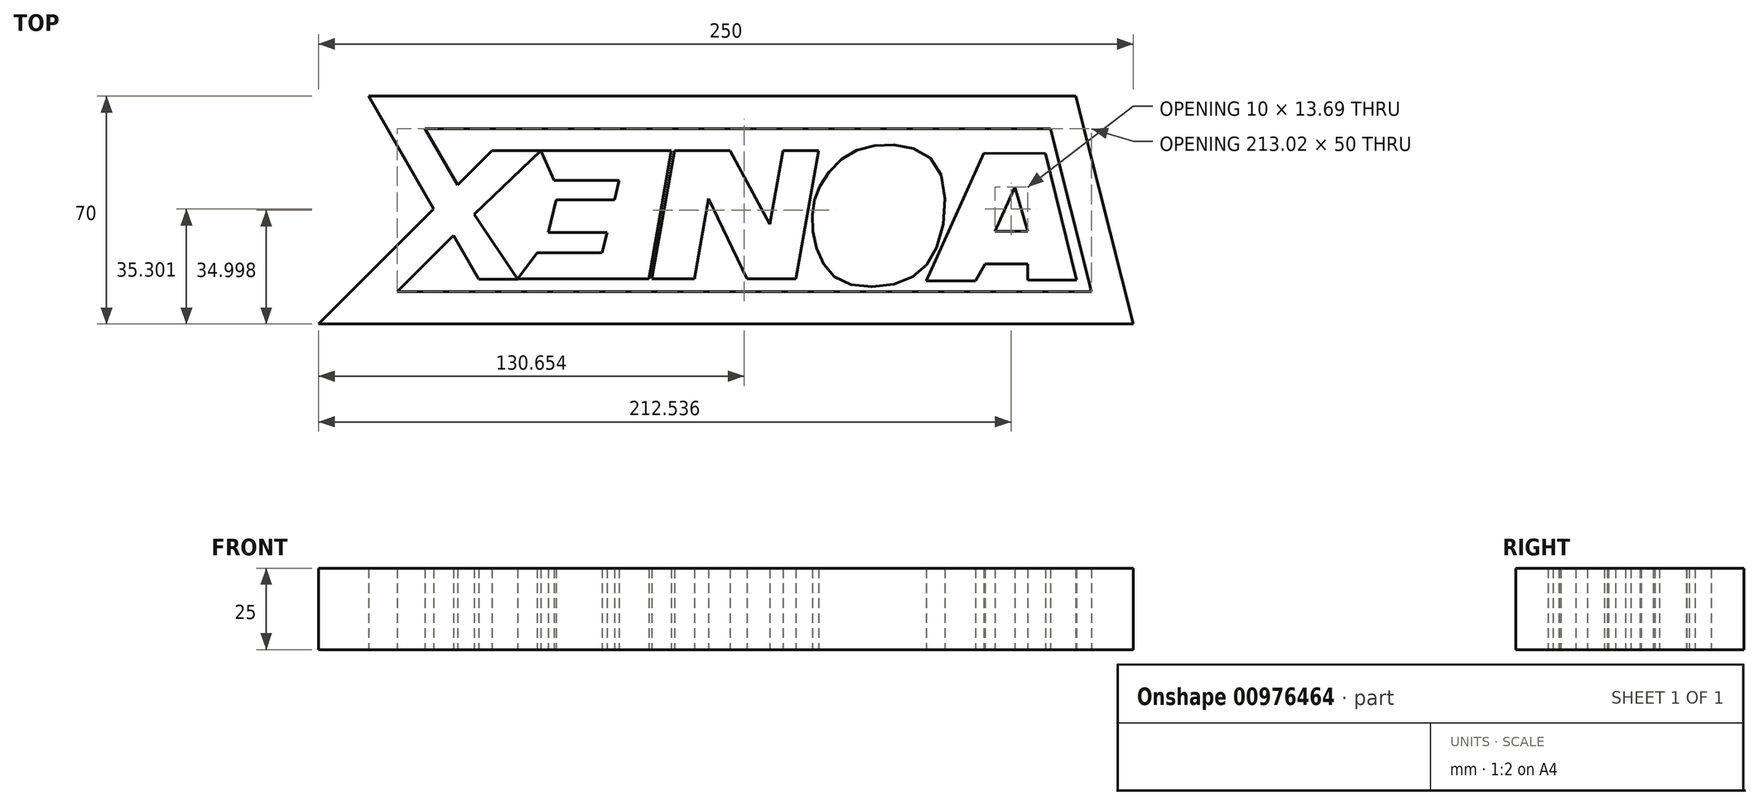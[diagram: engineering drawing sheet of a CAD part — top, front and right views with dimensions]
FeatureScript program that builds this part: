
annotation { "Feature Type Name" : "Feature", "Feature Type Description" : "" }
export const myFeature = defineFeature(function(context is Context, id is Id, definition is map)
    precondition{}
    {
        {
            var Q0;
            Q0=qCreatedBy(makeId("Top.planeOp"),FACE);
            var sketch = newSketch(context, id + "F0", { "sketchPlane" : qUnion([Q0])});
            skLineSegment(sketch, "E0", {"start": v(0, 0) * mm, "end": v(250, 0) * mm});
            skLineSegment(sketch, "E1", {"start": v(0, 0) * mm, "end": v(35.36, 35.36) * mm});
            skLineSegment(sketch, "E2", {"start": v(35.36, 35.36) * mm, "end": v(15.36, 70) * mm});
            skLineSegment(sketch, "E3", {"start": v(15.36, 70) * mm, "end": v(232.36, 70) * mm});
            skLineSegment(sketch, "E4", {"start": v(232.36, 70) * mm, "end": v(250, 0) * mm});
            skLineSegment(sketch, "E5.0", {"start": v(224.56, 60) * mm, "end": v(237.17, 10) * mm});
            skLineSegment(sketch, "E5.1", {"start": v(32.68, 60) * mm, "end": v(224.56, 60) * mm});
            skLineSegment(sketch, "E5.2", {"start": v(24.14, 10) * mm, "end": v(237.17, 10) * mm});
            skLineSegment(sketch, "E5.3", {"start": v(24.14, 10) * mm, "end": v(47.85, 33.71) * mm});
            skLineSegment(sketch, "E5.4", {"start": v(47.85, 33.71) * mm, "end": v(32.68, 60) * mm});
            skLineSegment(sketch, "E6", {"start": v(42.68, 42.68) * mm, "end": v(53.28, 53.28) * mm});
            skLineSegment(sketch, "E7", {"start": v(53.28, 53.28) * mm, "end": v(68.28, 53.28) * mm});
            skLineSegment(sketch, "E8", {"start": v(68.28, 53.28) * mm, "end": v(47.85, 33.71) * mm});
            skLineSegment(sketch, "E9", {"start": v(47.85, 33.71) * mm, "end": v(61.2, 13.76) * mm});
            skLineSegment(sketch, "E10", {"start": v(61.2, 13.76) * mm, "end": v(49.2, 13.76) * mm});
            skLineSegment(sketch, "E11", {"start": v(49.2, 13.76) * mm, "end": v(41.4, 27.26) * mm});
            skLineSegment(sketch, "E12", {"start": v(68.28, 53.28) * mm, "end": v(108.28, 53.28) * mm});
            skLineSegment(sketch, "E13", {"start": v(108.28, 53.28) * mm, "end": v(101.34, 13.9) * mm});
            skLineSegment(sketch, "E14", {"start": v(101.34, 13.9) * mm, "end": v(61.2, 13.9) * mm});
            skLineSegment(sketch, "E15", {"start": v(61.2, 13.9) * mm, "end": v(67.1, 21.96) * mm});
            skLineSegment(sketch, "E16", {"start": v(68.28, 53.28) * mm, "end": v(72.31, 44.13) * mm});
            skLineSegment(sketch, "E17", {"start": v(72.31, 44.13) * mm, "end": v(92.31, 44.13) * mm});
            skLineSegment(sketch, "E18", {"start": v(67.1, 21.96) * mm, "end": v(87.1, 21.96) * mm});
            skLineSegment(sketch, "E19", {"start": v(108.28, 53.28) * mm, "end": v(109.28, 53.28) * mm});
            skLineSegment(sketch, "E20", {"start": v(101.34, 13.9) * mm, "end": v(102.34, 13.9) * mm});
            skLineSegment(sketch, "E21", {"start": v(102.34, 13.9) * mm, "end": v(109.28, 53.28) * mm});
            skLineSegment(sketch, "E22", {"start": v(109.28, 53.28) * mm, "end": v(126.28, 53.28) * mm});
            skLineSegment(sketch, "E23", {"start": v(102.34, 13.9) * mm, "end": v(115.34, 13.9) * mm});
            skLineSegment(sketch, "E24", {"start": v(115.34, 13.9) * mm, "end": v(119.68, 38.51) * mm});
            skLineSegment(sketch, "E25", {"start": v(119.68, 38.51) * mm, "end": v(131.54, 13.92) * mm});
            skLineSegment(sketch, "E26", {"start": v(131.54, 13.92) * mm, "end": v(146.54, 13.92) * mm});
            skLineSegment(sketch, "E27", {"start": v(146.54, 13.92) * mm, "end": v(153.48, 53.31) * mm});
            skLineSegment(sketch, "E28", {"start": v(142.52, 53.31) * mm, "end": v(138.53, 30.66) * mm});
            skLineSegment(sketch, "E29", {"start": v(138.53, 30.66) * mm, "end": v(126.28, 53.28) * mm});
            skLineSegment(sketch, "E30", {"start": v(92.31, 44.13) * mm, "end": v(87.1, 21.96) * mm});
            skPoint(sketch, "E31", {"position": v(89.73, 33.13) * mm});
            skPoint(sketch, "E32", {"position": v(90.9, 38.13) * mm});
            skPoint(sketch, "E33", {"position": v(88.55, 28.13) * mm});
            skLineSegment(sketch, "E34", {"start": v(90.9, 38.13) * mm, "end": v(72.9, 38.13) * mm});
            skLineSegment(sketch, "E35", {"start": v(88.55, 28.13) * mm, "end": v(70.55, 28.13) * mm});
            skLineSegment(sketch, "E36", {"start": v(70.55, 28.13) * mm, "end": v(72.9, 38.13) * mm});
            skPoint(sketch, "E37", {"position": v(150, 33.62) * mm});
            skLineSegment(sketch, "E38", {"start": v(142.52, 53.31) * mm, "end": v(153.48, 53.31) * mm});
            skLineSegment(sketch, "E39", {"start": v(223.08, 52.32) * mm, "end": v(232.54, 13.45) * mm});
            skLineSegment(sketch, "E40", {"start": v(232.54, 13.45) * mm, "end": v(217.54, 13.45) * mm});
            skLineSegment(sketch, "E41", {"start": v(217.54, 13.45) * mm, "end": v(217.54, 18.45) * mm});
            skLineSegment(sketch, "E42", {"start": v(217.54, 18.45) * mm, "end": v(204.54, 18.45) * mm});
            skLineSegment(sketch, "E43", {"start": v(204.54, 18.45) * mm, "end": v(201.54, 13.26) * mm});
            skLineSegment(sketch, "E44", {"start": v(201.54, 13.26) * mm, "end": v(186.54, 13.26) * mm});
            skLineSegment(sketch, "E45", {"start": v(186.54, 13.26) * mm, "end": v(204.08, 52.51) * mm});
            skLineSegment(sketch, "E46", {"start": v(204.08, 52.51) * mm, "end": v(223.08, 52.32) * mm});
            skLineSegment(sketch, "E47", {"start": v(217.54, 18.45) * mm, "end": v(217.54, 28.45) * mm});
            skLineSegment(sketch, "E48", {"start": v(217.54, 28.45) * mm, "end": v(207.54, 28.45) * mm});
            skLineSegment(sketch, "E49", {"start": v(207.54, 28.45) * mm, "end": v(213.66, 42.15) * mm});
            skLineSegment(sketch, "E50", {"start": v(213.66, 42.15) * mm, "end": v(217.54, 28.45) * mm});
            skFitSpline(sketch, "E51", {"points": [v(151.53, 33.62) * mm, v(153.96, 42.44) * mm, v(162.22, 51.87) * mm, v(176.24, 55.02) * mm, v(189.9, 48.28) * mm, v(190.07, 24.56) * mm, v(179.83, 13.34) * mm, v(161.41, 12.8) * mm, v(153.5, 21.42) * mm, v(151.53, 33.62) * mm]});
            skFitSpline(sketch, "E52.0", {"points": [v(161.5, 32.03) * mm, v(161.5, 33.17) * mm, v(161.6, 34.1) * mm, v(161.72, 34.9) * mm, v(161.9, 35.62) * mm, v(162.1, 36.23) * mm, v(162.32, 36.76) * mm, v(162.51, 37.2) * mm, v(162.74, 37.66) * mm, v(163.1, 38.33) * mm, v(163.6, 39.18) * mm, v(164.29, 40.2) * mm, v(165.04, 41.16) * mm, v(165.83, 42.02) * mm, v(166.5, 42.63) * mm, v(167.02, 43.04) * mm, v(167.4, 43.32) * mm, v(167.76, 43.55) * mm, v(168.15, 43.77) * mm, v(168.57, 43.97) * mm, v(169.16, 44.23) * mm, v(169.98, 44.52) * mm, v(171.09, 44.8) * mm, v(172.32, 44.98) * mm, v(173.66, 45.08) * mm, v(174.73, 45.08) * mm, v(175.47, 45.05) * mm, v(175.97, 45.02) * mm, v(176.58, 44.96) * mm, v(177.28, 44.87) * mm, v(178.15, 44.72) * mm, v(179.13, 44.48) * mm, v(180.04, 44.14) * mm, v(180.66, 43.8) * mm, v(180.95, 43.58) * mm, v(181.1, 43.43) * mm, v(181.19, 43.33) * mm, v(181.25, 43.24) * mm, v(181.3, 43.16) * mm, v(181.36, 43.06) * mm, v(181.42, 42.92) * mm, v(181.52, 42.7) * mm, v(181.7, 42.18) * mm, v(181.98, 41.11) * mm, v(182.2, 39.44) * mm, v(182.28, 37.48) * mm, v(182.2, 35.37) * mm, v(181.95, 33.2) * mm, v(181.56, 31.09) * mm, v(181.07, 29.13) * mm, v(180.5, 27.45) * mm, v(179.93, 26.15) * mm, v(179.38, 25.18) * mm, v(178.87, 24.48) * mm, v(178.37, 23.95) * mm, v(177.83, 23.5) * mm, v(177.14, 23.07) * mm, v(176.21, 22.64) * mm, v(174.96, 22.2) * mm, v(173.46, 21.83) * mm, v(171.82, 21.57) * mm, v(170.14, 21.44) * mm, v(168.53, 21.45) * mm, v(167.32, 21.56) * mm, v(166.48, 21.7) * mm, v(165.94, 21.82) * mm, v(165.57, 21.92) * mm, v(165.33, 22) * mm, v(165.17, 22.06) * mm, v(165.05, 22.11) * mm, v(164.9, 22.18) * mm, v(164.74, 22.27) * mm, v(164.57, 22.37) * mm, v(164.38, 22.52) * mm, v(164.13, 22.75) * mm, v(163.8, 23.16) * mm, v(163.4, 23.77) * mm, v(163, 24.6) * mm, v(162.58, 25.68) * mm, v(162.21, 26.88) * mm, v(161.81, 28.59) * mm, v(161.57, 30.37) * mm, v(161.5, 32.03) * mm, v(161.5, 33.17) * mm, v(161.6, 34.1) * mm, v(161.5, 32.03) * mm]});
            skLineSegment(sketch, "E53", {"start": v(179.1, 44.47) * mm, "end": v(162.82, 25.07) * mm});
            skLineSegment(sketch, "E54", {"start": v(181.97, 41) * mm, "end": v(165.9, 21.83) * mm});
            skSolve(sketch);
        }
        {
            var Q0;
            Q0=makeQuery(id+"F0.imprint","IMPRINT",FACE,{"disambiguationData":[TD([[makeQuery(id+"F0.imprint","IMPRINT",EDGE,{"derivedFrom":sQuery(id+"F0.wireOp",EDGE,"E0")}),1.0]])]});
            var Q1;
            {var subQ2=sQuery(id+"F0.wireOp",EDGE,"E6");Q1=makeQuery(id+"F0.imprint","IMPRINT",FACE,{"disambiguationData":[TD([[makeQuery(id+"F0.imprint","IMPRINT",EDGE,{"derivedFrom":subQ2}),-1.0]])]});}
            var Q2;
            {var subQ0=sQuery(id+"F0.wireOp",EDGE,"E9");Q2=makeQuery(id+"F0.imprint","IMPRINT",FACE,{"disambiguationData":[TD([[makeQuery(id+"F0.imprint","IMPRINT",EDGE,{"derivedFrom":subQ0}),-1.0]])]});}
            var Q3;
            {var subQ0=sQuery(id+"F0.wireOp",EDGE,"E34");Q3=makeQuery(id+"F0.imprint","IMPRINT",FACE,{"disambiguationData":[TD([[makeQuery(id+"F0.imprint","IMPRINT",EDGE,{"derivedFrom":subQ0}),1.0]])]});}
            var Q4;
            Q4=makeQuery(id+"F0.imprint","IMPRINT",FACE,{"disambiguationData":[TD([[makeQuery(id+"F0.imprint","IMPRINT",EDGE,{"derivedFrom":sQuery(id+"F0.wireOp",EDGE,"E12")}),-1.0]])]});
            var Q5;
            Q5=makeQuery(id+"F0.imprint","IMPRINT",FACE,{"disambiguationData":[TD([[makeQuery(id+"F0.imprint","IMPRINT",EDGE,{"derivedFrom":sQuery(id+"F0.wireOp",EDGE,"E21")}),-1.0]])]});
            var Q6;
            Q6=makeQuery(id+"F0.imprint","IMPRINT",FACE,{"disambiguationData":[TD([[makeQuery(id+"F0.imprint","IMPRINT",EDGE,{"derivedFrom":sQuery(id+"F0.wireOp",EDGE,"E51")}),-1.0]])]});
            var Q7;
            {var subQ0=sQuery(id+"F0.wireOp",EDGE,"E53");Q7=makeQuery(id+"F0.imprint","IMPRINT",FACE,{"disambiguationData":[TD([[makeQuery(id+"F0.imprint","IMPRINT",EDGE,{"derivedFrom":subQ0}),1.0]])]});}
            var Q8;
            Q8=makeQuery(id+"F0.imprint","IMPRINT",FACE,{"disambiguationData":[TD([[makeQuery(id+"F0.imprint","IMPRINT",EDGE,{"derivedFrom":sQuery(id+"F0.wireOp",EDGE,"E39")}),-1.0]])]});
            var Q9;
            {var subQ0=sQuery(id+"F0.wireOp",EDGE,"JfNl9Xfk-aqaR-qNYz-ximk-0m5AAW0ROm31");Q9=makeQuery(id+"F0.imprint","IMPRINT",FACE,{"disambiguationData":[TD([[makeQuery(id+"F0.imprint","IMPRINT",EDGE,{"derivedFrom":subQ0}),-1.0]])]});}
            var Q10;
            {var subQ0=sQuery(id+"F0.wireOp",EDGE,"E15");var subQ1=sQuery(id+"F0.wireOp",EDGE,"E14");var subQ2=makeQuery(id+"F0.imprint","INTERSECT",VERTEX,{"derivedFrom":[subQ1,subQ0]});Q10=makeQuery(id+"F0.imprint","IMPRINT",FACE,{"disambiguationData":[TD([[makeQuery(id+"F0.imprint","IMPRINT",EDGE,{"disambiguationData":[TD([[subQ2,1.0]])],"derivedFrom":subQ1}),-1.0]])]});}
            var Q11;
            {var subQ3=sQuery(id+"F0.wireOp",EDGE,"eN30COPq-oqJq-rnKl-EqHf-OhdowSKKRAAw");Q11=makeQuery(id+"F0.imprint","IMPRINT",FACE,{"disambiguationData":[TD([[makeQuery(id+"F0.imprint","IMPRINT",EDGE,{"derivedFrom":subQ3}),1.0]])]});}
            var Q12;
            {var subQ0=sQuery(id+"F0.wireOp",EDGE,"imM2ijot-e2D8-q0Y7-5tzL-eRpiLB6fCpNz");Q12=makeQuery(id+"F0.imprint","IMPRINT",FACE,{"disambiguationData":[TD([[makeQuery(id+"F0.imprint","IMPRINT",EDGE,{"derivedFrom":subQ0}),-1.0]])]});}
            var Q13;
            {var subQ0=sQuery(id+"F0.wireOp",EDGE,"RDafbrLf-kzFO-E4ZM-40qh-3E63GRLbKq8Y");Q13=makeQuery(id+"F0.imprint","IMPRINT",FACE,{"disambiguationData":[TD([[makeQuery(id+"F0.imprint","IMPRINT",EDGE,{"derivedFrom":subQ0}),-1.0]])]});}
            var Q14;
            {var subQ0=sQuery(id+"F0.wireOp",EDGE,"6cAeuiRb-naha-nZBh-ziNz-JyJCdYFGemb1");Q14=makeQuery(id+"F0.imprint","IMPRINT",FACE,{"disambiguationData":[TD([[makeQuery(id+"F0.imprint","IMPRINT",EDGE,{"derivedFrom":subQ0}),-1.0]])]});}
            var Q15;
            {var subQ0=sQuery(id+"F0.wireOp",EDGE,"ylp7s7nb-VYOC-vkmB-fRLy-HwE1BUQnb8ae");Q15=makeQuery(id+"F0.imprint","IMPRINT",FACE,{"disambiguationData":[TD([[makeQuery(id+"F0.imprint","IMPRINT",EDGE,{"derivedFrom":subQ0}),-1.0]])]});}
            var Q16;
            {var subQ0=sQuery(id+"F0.wireOp",EDGE,"D8vqczcZ-tITf-OYWz-xtXg-1sGLX5qLOuWc");Q16=makeQuery(id+"F0.imprint","IMPRINT",FACE,{"disambiguationData":[TD([[makeQuery(id+"F0.imprint","IMPRINT",EDGE,{"derivedFrom":subQ0}),-1.0]])]});}
            extrude(context, id + "F1", {"entities" : qUnion([Q0, Q1, Q2, Q3, Q4, Q5, Q6, Q7, Q8, Q9, Q10, Q11, Q12, Q13, Q14, Q15, Q16]), "depth" : 25 * mm, "offsetDistance" : 25 * mm});
        }
    });
